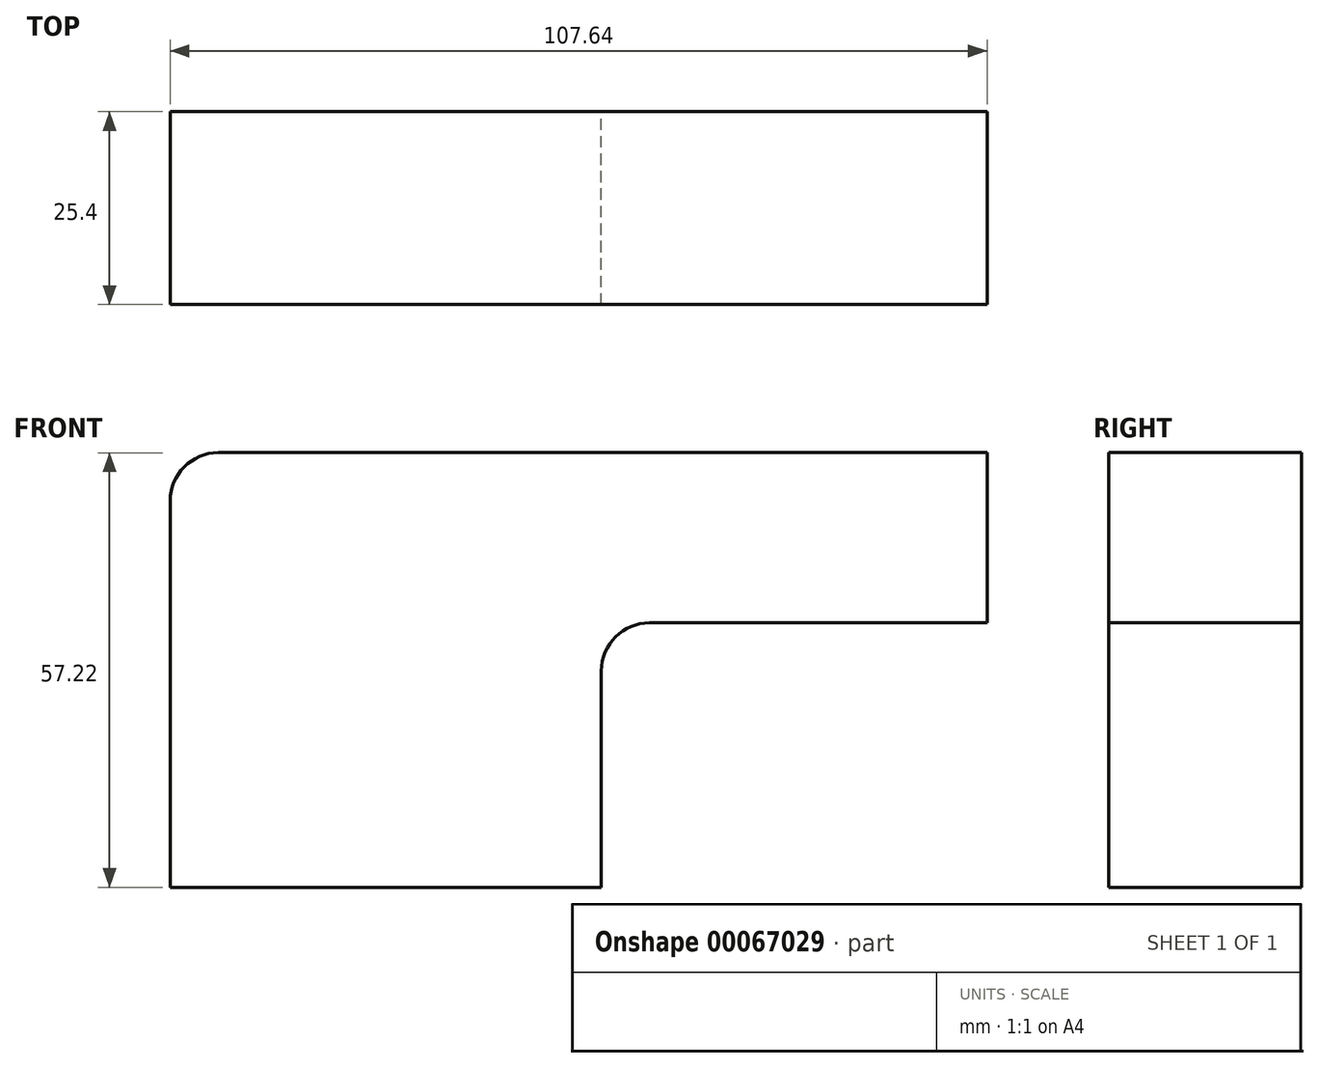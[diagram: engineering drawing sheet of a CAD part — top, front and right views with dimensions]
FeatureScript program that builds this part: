
annotation { "Feature Type Name" : "Feature", "Feature Type Description" : "" }
export const myFeature = defineFeature(function(context is Context, id is Id, definition is map)
    precondition{}
    {
        {
            var Q0;
            Q0=qCreatedBy(makeId("Front.planeOp"),FACE);
            var sketch = newSketch(context, id + "F0", { "sketchPlane" : qUnion([Q0])});
            skLineSegment(sketch, "E0", {"start": v(-107.64, 16.04) * mm, "end": v(-107.64, -34.83) * mm});
            skLineSegment(sketch, "E1", {"start": v(-107.64, -34.83) * mm, "end": v(-50.82, -34.83) * mm});
            skLineSegment(sketch, "E2", {"start": v(-50.82, -34.83) * mm, "end": v(-50.82, -6.35) * mm});
            skLineSegment(sketch, "E3", {"start": v(-44.47, 0) * mm, "end": v(0, 0) * mm});
            skLineSegment(sketch, "E4", {"start": v(0, 0) * mm, "end": v(0, 22.4) * mm});
            skLineSegment(sketch, "E5", {"start": v(0, 22.4) * mm, "end": v(-101.3, 22.4) * mm});
            skPoint(sketch, "E6.visualSharp", {"position": v(-107.64, 22.4) * mm});
            skArc(sketch, "E6.filletArc", {"start": v(-101.3, 22.4) * mm, "mid": v(-105.78, 20.53) * mm, "end": v(-107.64, 16.04) * mm});
            skPoint(sketch, "E7.visualSharp", {"position": v(-50.82, 0) * mm});
            skArc(sketch, "E7.filletArc", {"start": v(-44.47, 0) * mm, "mid": v(-48.96, -1.86) * mm, "end": v(-50.82, -6.35) * mm});
            skSolve(sketch);
        }
        {
            var Q0;
            Q0 = qSketchRegion(id + "F0", true);
            extrude(context, id + "F1", {"entities" : qUnion([Q0]), "depth" : 25.4 * mm});
        }
    });
